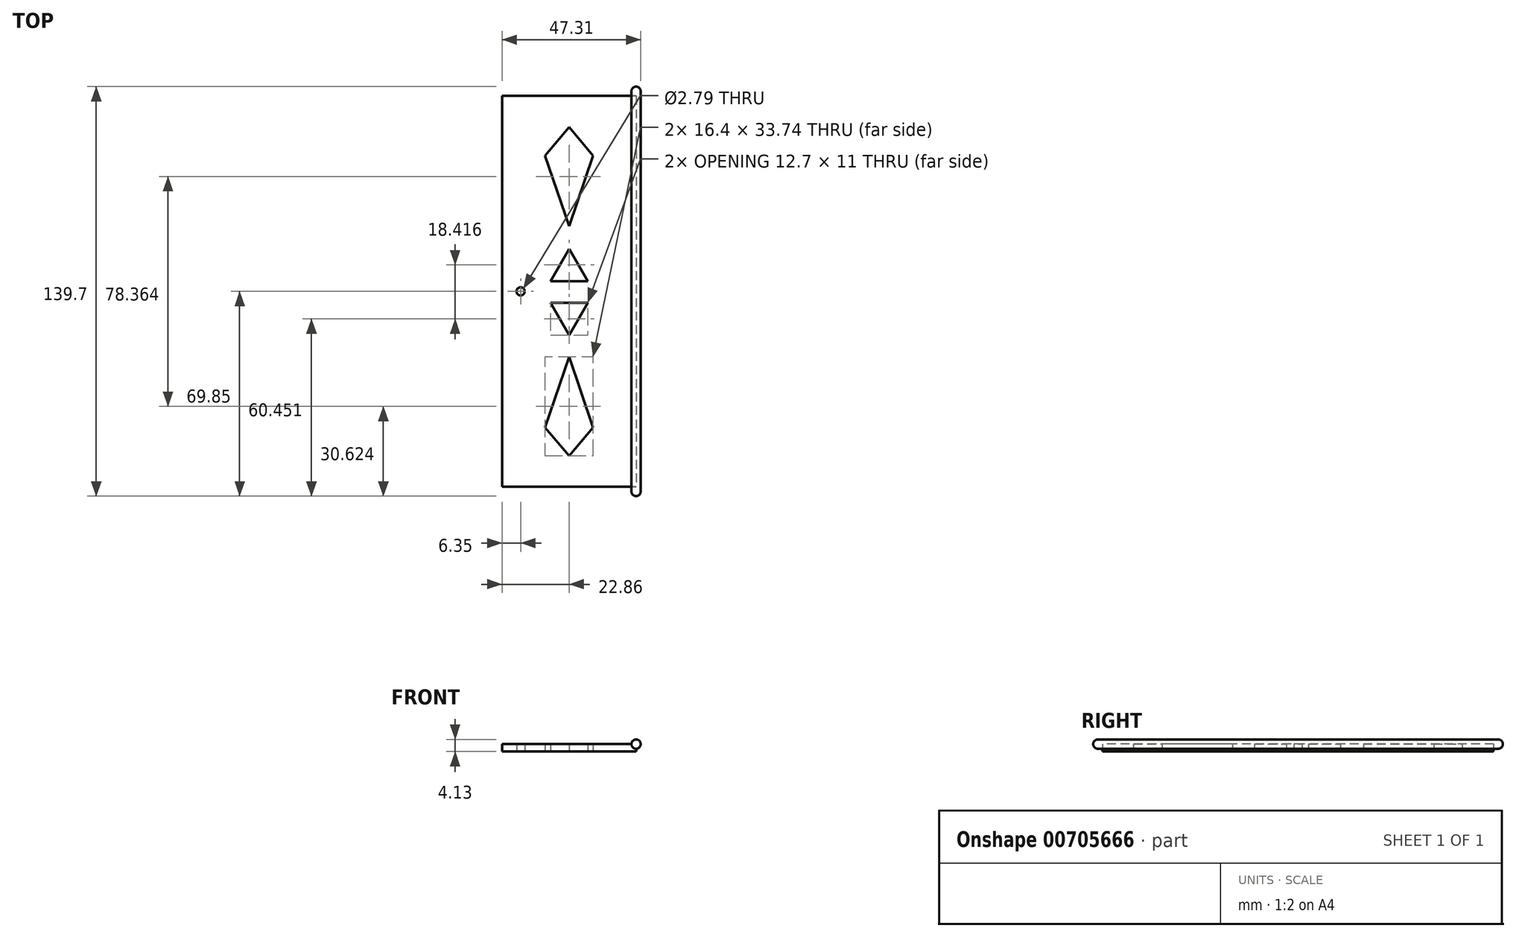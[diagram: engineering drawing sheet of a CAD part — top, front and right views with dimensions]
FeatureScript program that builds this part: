
annotation { "Feature Type Name" : "Feature", "Feature Type Description" : "" }
export const myFeature = defineFeature(function(context is Context, id is Id, definition is map)
    precondition{}
    {
        {
            var Q0;
            Q0=qCreatedBy(makeId("Top.planeOp"),FACE);
            var sketch = newSketch(context, id + "F0", { "sketchPlane" : qUnion([Q0])});
            skLineSegment(sketch, "E0.bottom", {"start": v(22.86, 66.68) * mm, "end": v(-22.86, 66.68) * mm});
            skLineSegment(sketch, "E0.top", {"start": v(22.86, -66.68) * mm, "end": v(-22.86, -66.68) * mm});
            skLineSegment(sketch, "E0.left", {"start": v(22.86, 66.68) * mm, "end": v(22.86, -66.68) * mm});
            skLineSegment(sketch, "E0.right", {"start": v(-22.86, 66.68) * mm, "end": v(-22.86, -66.68) * mm});
            skPoint(sketch, "E0.middle", {"position": v(0, 0) * mm});
            skSolve(sketch);
        }
        {
            var Q0;
            Q0 = qSketchRegion(id + "F0", true);
            extrude(context, id + "F1", {"entities" : qUnion([Q0]), "depth" : 2.54 * mm, "offsetDistance" : 25.4 * mm});
        }
        {
            var Q0;
            Q0=makeQuery(id+"F1.opExtrude","SWEPT_FACE",FACE,{"disambiguationData":[OSD([sQuery(id+"F0.wireOp",EDGE,"E0.top")])]});
            var sketch = newSketch(context, id + "F2", { "sketchPlane" : qUnion([Q0])});
            skCircle(sketch, "E1", {"center": v(22.86, 2.54) * mm, "radius": 1.59 * mm});
            skSolve(sketch);
        }
        {
            var Q0;
            Q0 = qSketchRegion(id + "F2", true);
            extrude(context, id + "F3", {"entities" : qUnion([Q0]), "operationType" : NewBodyOperationType.ADD, "oppositeDirection" : true, "depth" : 136.53 * mm, "offsetDistance" : 25.4 * mm});
        }
        {
            var Q0;
            Q0 = qSketchRegion(id + "F2", true);
            extrude(context, id + "F4", {"entities" : qUnion([Q0]), "operationType" : NewBodyOperationType.ADD, "depth" : 3.17 * mm, "offsetDistance" : 25.4 * mm});
        }
        {
            var Q0;
            Q0=makeQuery(id+"F4.opExtrude","CAP_FACE",FACE,{"disambiguationData":[OSD([sQuery(id+"F2.wireOp",EDGE,"E1")])],"isStart":false});
            var Q1;
            Q1=makeQuery(id+"F3.opExtrude","CAP_FACE",FACE,{"disambiguationData":[OSD([sQuery(id+"F2.wireOp",EDGE,"E1")])],"isStart":false});
            fillet(context, id + "F5", {"entities" : qUnion([Q0, Q1]), "radius" : 1.59 * mm, "tangentPropagation" : true, "allowEdgeOverflow" : false});
        }
        {
            var Q0;
            Q0=makeQuery(id+"F1.opExtrude","CAP_FACE",FACE,{"disambiguationData":[OSD([sQuery(id+"F0.wireOp",EDGE,"E0.bottom"),sQuery(id+"F0.wireOp",EDGE,"E0.top"),sQuery(id+"F0.wireOp",EDGE,"E0.left"),sQuery(id+"F0.wireOp",EDGE,"E0.right")])],"isStart":true});
            var sketch = newSketch(context, id + "F6", { "sketchPlane" : qUnion([Q0])});
            skLineSegment(sketch, "E2", {"start": v(-22.86, 0) * mm, "end": v(-16.51, 0) * mm});
            skCircle(sketch, "E3", {"center": v(-16.51, 0) * mm, "radius": 1.4 * mm});
            skSolve(sketch);
        }
        {
            var Q0;
            Q0 = qSketchRegion(id + "F6", true);
            extrude(context, id + "F7", {"entities" : qUnion([Q0]), "operationType" : NewBodyOperationType.REMOVE, "oppositeDirection" : true, "depth" : 25.4 * mm, "offsetDistance" : 25.4 * mm});
        }
        {
            var Q0;
            Q0=makeQuery(id+"F1.opExtrude","CAP_FACE",FACE,{"disambiguationData":[OSD([sQuery(id+"F0.wireOp",EDGE,"E0.bottom"),sQuery(id+"F0.wireOp",EDGE,"E0.top"),sQuery(id+"F0.wireOp",EDGE,"E0.left"),sQuery(id+"F0.wireOp",EDGE,"E0.right")])],"isStart":true});
            var sketch = newSketch(context, id + "F8", { "sketchPlane" : qUnion([Q0])});
            skLineSegment(sketch, "E4", {"start": v(0, 56.1) * mm, "end": v(-8.2, 46.4) * mm});
            skLineSegment(sketch, "E5", {"start": v(-8.2, 46.4) * mm, "end": v(0, 22.36) * mm});
            skLineSegment(sketch, "E6", {"start": v(0, 22.36) * mm, "end": v(8.2, 46.4) * mm});
            skLineSegment(sketch, "E7", {"start": v(8.2, 46.4) * mm, "end": v(0, 56.1) * mm});
            skLineSegment(sketch, "E8", {"start": v(0, -56) * mm, "end": v(-8.2, -46.31) * mm});
            skLineSegment(sketch, "E9", {"start": v(-8.2, -46.31) * mm, "end": v(0, -22.27) * mm});
            skLineSegment(sketch, "E10", {"start": v(0, -22.27) * mm, "end": v(8.2, -46.31) * mm});
            skLineSegment(sketch, "E11", {"start": v(8.2, -46.31) * mm, "end": v(0, -56) * mm});
            skLineSegment(sketch, "E12", {"start": v(0, -14.52) * mm, "end": v(-6.35, -3.52) * mm});
            skLineSegment(sketch, "E13", {"start": v(-6.35, -3.52) * mm, "end": v(6.35, -3.52) * mm});
            skLineSegment(sketch, "E14", {"start": v(6.35, -3.52) * mm, "end": v(0, -14.52) * mm});
            skLineSegment(sketch, "E15", {"start": v(0, 14.9) * mm, "end": v(-6.35, 3.9) * mm});
            skLineSegment(sketch, "E16", {"start": v(-6.35, 3.9) * mm, "end": v(6.35, 3.9) * mm});
            skLineSegment(sketch, "E17", {"start": v(6.35, 3.9) * mm, "end": v(0, 14.9) * mm});
            skSolve(sketch);
        }
        {
            var Q0;
            Q0 = qSketchRegion(id + "F8", true);
            extrude(context, id + "F9", {"entities" : qUnion([Q0]), "operationType" : NewBodyOperationType.REMOVE, "oppositeDirection" : true, "depth" : 25.4 * mm, "offsetDistance" : 25.4 * mm});
        }
    });
